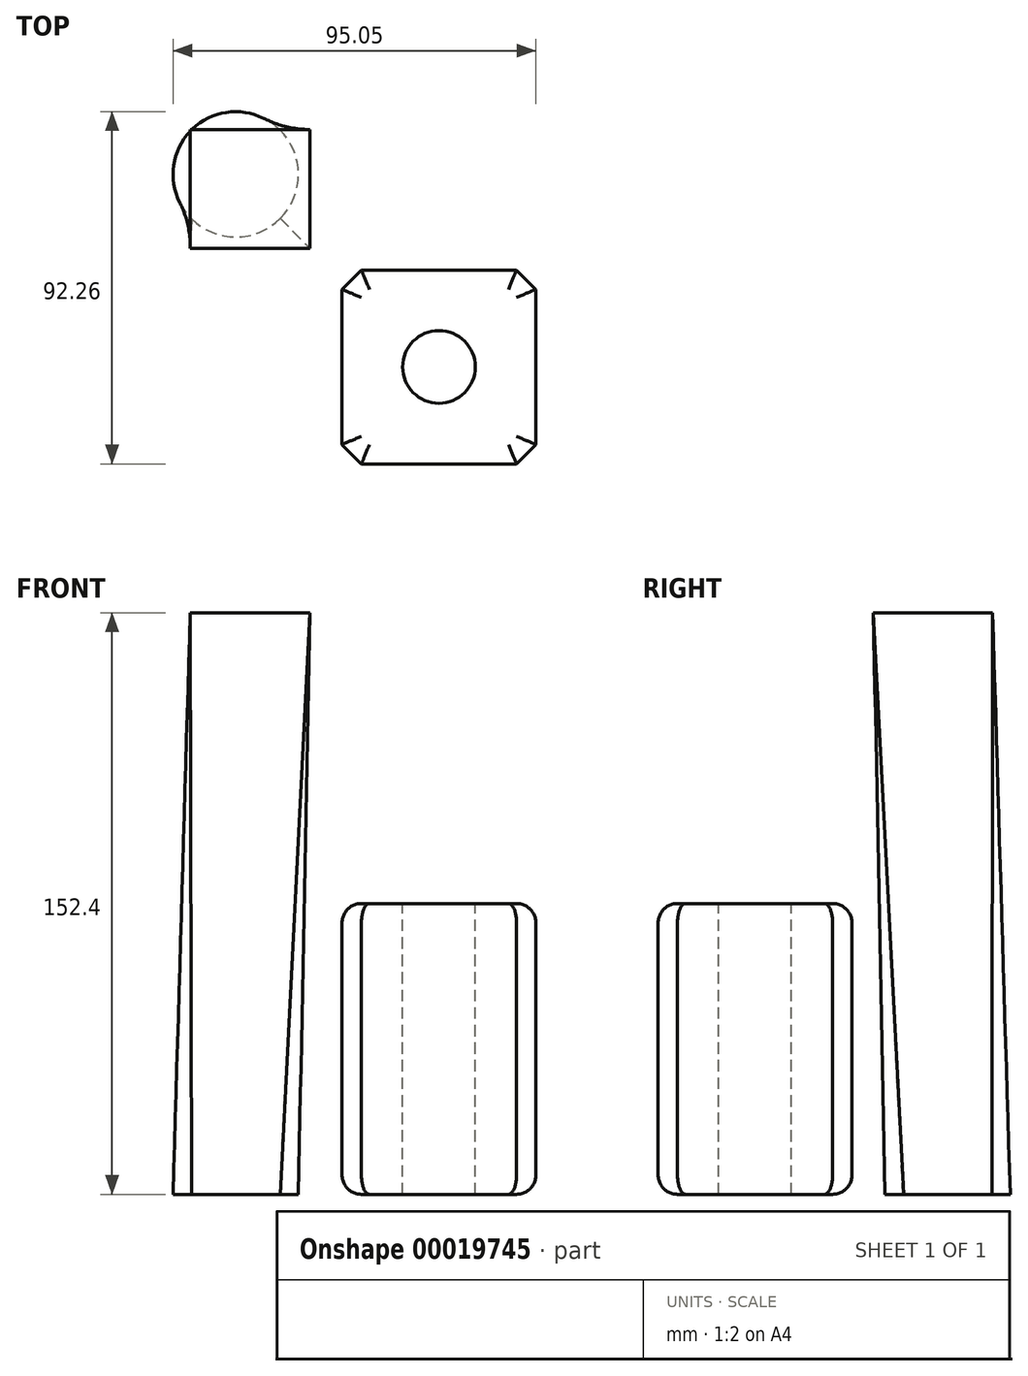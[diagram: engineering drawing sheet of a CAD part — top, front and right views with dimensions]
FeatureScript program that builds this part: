
annotation { "Feature Type Name" : "Feature", "Feature Type Description" : "" }
export const myFeature = defineFeature(function(context is Context, id is Id, definition is map)
    precondition{}
    {
        {
            var Q0;
            Q0=qCreatedBy(makeId("Top.planeOp"),FACE);
            var sketch = newSketch(context, id + "F0", { "sketchPlane" : qUnion([Q0])});
            skLineSegment(sketch, "E0.rect.bottom", {"start": v(-25.4, 25.4) * mm, "end": v(25.4, 25.4) * mm});
            skLineSegment(sketch, "E0.rect.top", {"start": v(-25.4, -25.4) * mm, "end": v(25.4, -25.4) * mm});
            skLineSegment(sketch, "E0.rect.left", {"start": v(-25.4, 25.4) * mm, "end": v(-25.4, -25.4) * mm});
            skLineSegment(sketch, "E0.rect.right", {"start": v(25.4, 25.4) * mm, "end": v(25.4, -25.4) * mm});
            skPoint(sketch, "E0.rect.middle", {"position": v(0, 0) * mm});
            skSolve(sketch);
        }
        {
            var Q0;
            Q0 = qSketchRegion(id + "F0", true);
            extrude(context, id + "F1", {"entities" : qUnion([Q0]), "depth" : 76.2 * mm});
        }
        {
            var Q0;
            Q0=makeQuery(id+"F1.opExtrude","CAP_FACE",FACE,{"disambiguationData":[OSD([sQuery(id+"F0.wireOp",EDGE,"E0.rect.bottom"),sQuery(id+"F0.wireOp",EDGE,"E0.rect.top"),sQuery(id+"F0.wireOp",EDGE,"E0.rect.left"),sQuery(id+"F0.wireOp",EDGE,"E0.rect.right")])],"isStart":false});
            var sketch = newSketch(context, id + "F2", { "sketchPlane" : qUnion([Q0])});
            skCircle(sketch, "E1", {"center": v(0, 0) * mm, "radius": 9.53 * mm});
            skSolve(sketch);
        }
        {
            var Q0;
            Q0=makeQuery(id+"F2.imprint","IMPRINT",FACE,{"disambiguationData":[TD([[makeQuery(id+"F2.imprint","IMPRINT",EDGE,{"derivedFrom":sQuery(id+"F2.wireOp",EDGE,"E1")}),1.0]])]});
            extrude(context, id + "F3", {"entities" : qUnion([Q0]), "operationType" : NewBodyOperationType.REMOVE, "oppositeDirection" : true, "depth" : 123.9 * mm});
        }
        {
            var Q0;
            Q0=makeQuery(id+"F1.opExtrude","SWEPT_EDGE",EDGE,{"disambiguationData":[OSD([sQuery(id+"F0.wireOp",EDGE,"E0.rect.top"),sQuery(id+"F0.wireOp",EDGE,"E0.rect.left")])]});
            var Q1;
            Q1=makeQuery(id+"F1.opExtrude","SWEPT_EDGE",EDGE,{"disambiguationData":[OSD([sQuery(id+"F0.wireOp",EDGE,"E0.rect.top"),sQuery(id+"F0.wireOp",EDGE,"E0.rect.right")])]});
            var Q2;
            Q2=makeQuery(id+"F1.opExtrude","SWEPT_EDGE",EDGE,{"disambiguationData":[OSD([sQuery(id+"F0.wireOp",EDGE,"E0.rect.bottom"),sQuery(id+"F0.wireOp",EDGE,"E0.rect.right")])]});
            var Q3;
            Q3=makeQuery(id+"F1.opExtrude","SWEPT_EDGE",EDGE,{"disambiguationData":[OSD([sQuery(id+"F0.wireOp",EDGE,"E0.rect.bottom"),sQuery(id+"F0.wireOp",EDGE,"E0.rect.left")])]});
            chamfer(context, id + "F4", {"entities" : qUnion([Q0, Q1, Q2, Q3]), "width" : 5.08 * mm, "tangentPropagation" : true});
        }
        {
            var Q0;
            Q0=makeQuery(id+"F1.opExtrude","CAP_EDGE",EDGE,{"disambiguationData":[OSD([sQuery(id+"F0.wireOp",EDGE,"E0.rect.bottom")])],"isStart":false});
            var Q1;
            {var subQ0=sQuery(id+"F0.wireOp",EDGE,"E0.rect.bottom");var subQ1=sQuery(id+"F0.wireOp",EDGE,"E0.rect.left");Q1=makeQuery(id+"F4.opChamfer","BLEND_EDGE",EDGE,{"blendedFrom":[makeQuery(id+"F1.opExtrude","SWEPT_EDGE",EDGE,{"disambiguationData":[OSD([subQ0,subQ1])]}),makeQuery(id+"F1.opExtrude","CAP_FACE",FACE,{"disambiguationData":[OSD([subQ0,sQuery(id+"F0.wireOp",EDGE,"E0.rect.top"),subQ1,sQuery(id+"F0.wireOp",EDGE,"E0.rect.right")])],"isStart":false})],"blendedInto":[makeQuery(id+"F1.opExtrude","CAP_FACE",FACE,{"disambiguationData":[OSD([subQ0,sQuery(id+"F0.wireOp",EDGE,"E0.rect.top"),subQ1,sQuery(id+"F0.wireOp",EDGE,"E0.rect.right")])],"isStart":false})]});}
            var Q2;
            Q2=makeQuery(id+"F1.opExtrude","CAP_EDGE",EDGE,{"disambiguationData":[OSD([sQuery(id+"F0.wireOp",EDGE,"E0.rect.left")])],"isStart":false});
            var Q3;
            Q3=makeQuery(id+"F1.opExtrude","CAP_EDGE",EDGE,{"disambiguationData":[OSD([sQuery(id+"F0.wireOp",EDGE,"E0.rect.top")])],"isStart":false});
            var Q4;
            Q4=makeQuery(id+"F1.opExtrude","CAP_EDGE",EDGE,{"disambiguationData":[OSD([sQuery(id+"F0.wireOp",EDGE,"E0.rect.right")])],"isStart":false});
            var Q5;
            {var subQ0=sQuery(id+"F0.wireOp",EDGE,"E0.rect.bottom");var subQ1=sQuery(id+"F0.wireOp",EDGE,"E0.rect.right");Q5=makeQuery(id+"F4.opChamfer","BLEND_EDGE",EDGE,{"blendedFrom":[makeQuery(id+"F1.opExtrude","SWEPT_EDGE",EDGE,{"disambiguationData":[OSD([subQ0,subQ1])]}),makeQuery(id+"F1.opExtrude","CAP_FACE",FACE,{"disambiguationData":[OSD([subQ0,sQuery(id+"F0.wireOp",EDGE,"E0.rect.top"),sQuery(id+"F0.wireOp",EDGE,"E0.rect.left"),subQ1])],"isStart":false})],"blendedInto":[makeQuery(id+"F1.opExtrude","CAP_FACE",FACE,{"disambiguationData":[OSD([subQ0,sQuery(id+"F0.wireOp",EDGE,"E0.rect.top"),sQuery(id+"F0.wireOp",EDGE,"E0.rect.left"),subQ1])],"isStart":false})]});}
            var Q6;
            {var subQ0=sQuery(id+"F0.wireOp",EDGE,"E0.rect.top");var subQ1=sQuery(id+"F0.wireOp",EDGE,"E0.rect.right");Q6=makeQuery(id+"F4.opChamfer","BLEND_EDGE",EDGE,{"blendedFrom":[makeQuery(id+"F1.opExtrude","SWEPT_EDGE",EDGE,{"disambiguationData":[OSD([subQ0,subQ1])]}),makeQuery(id+"F1.opExtrude","CAP_FACE",FACE,{"disambiguationData":[OSD([sQuery(id+"F0.wireOp",EDGE,"E0.rect.bottom"),subQ0,sQuery(id+"F0.wireOp",EDGE,"E0.rect.left"),subQ1])],"isStart":false})],"blendedInto":[makeQuery(id+"F1.opExtrude","CAP_FACE",FACE,{"disambiguationData":[OSD([sQuery(id+"F0.wireOp",EDGE,"E0.rect.bottom"),subQ0,sQuery(id+"F0.wireOp",EDGE,"E0.rect.left"),subQ1])],"isStart":false})]});}
            var Q7;
            {var subQ0=sQuery(id+"F0.wireOp",EDGE,"E0.rect.top");var subQ1=sQuery(id+"F0.wireOp",EDGE,"E0.rect.left");Q7=makeQuery(id+"F4.opChamfer","BLEND_EDGE",EDGE,{"blendedFrom":[makeQuery(id+"F1.opExtrude","SWEPT_EDGE",EDGE,{"disambiguationData":[OSD([subQ0,subQ1])]}),makeQuery(id+"F1.opExtrude","CAP_FACE",FACE,{"disambiguationData":[OSD([sQuery(id+"F0.wireOp",EDGE,"E0.rect.bottom"),subQ0,subQ1,sQuery(id+"F0.wireOp",EDGE,"E0.rect.right")])],"isStart":false})],"blendedInto":[makeQuery(id+"F1.opExtrude","CAP_FACE",FACE,{"disambiguationData":[OSD([sQuery(id+"F0.wireOp",EDGE,"E0.rect.bottom"),subQ0,subQ1,sQuery(id+"F0.wireOp",EDGE,"E0.rect.right")])],"isStart":false})]});}
            fillet(context, id + "F5", {"entities" : qUnion([Q0, Q1, Q2, Q3, Q4, Q5, Q6, Q7]), "radius" : 5.08 * mm, "tangentPropagation" : true, "allowEdgeOverflow" : false});
        }
        {
            var Q0;
            {var subQ0=sQuery(id+"F0.wireOp",EDGE,"E0.rect.top");var subQ1=sQuery(id+"F0.wireOp",EDGE,"E0.rect.left");Q0=makeQuery(id+"F4.opChamfer","BLEND_EDGE",EDGE,{"blendedFrom":[makeQuery(id+"F1.opExtrude","SWEPT_EDGE",EDGE,{"disambiguationData":[OSD([subQ0,subQ1])]}),makeQuery(id+"F1.opExtrude","CAP_FACE",FACE,{"disambiguationData":[OSD([sQuery(id+"F0.wireOp",EDGE,"E0.rect.bottom"),subQ0,subQ1,sQuery(id+"F0.wireOp",EDGE,"E0.rect.right")])],"isStart":true})],"blendedInto":[makeQuery(id+"F1.opExtrude","CAP_FACE",FACE,{"disambiguationData":[OSD([sQuery(id+"F0.wireOp",EDGE,"E0.rect.bottom"),subQ0,subQ1,sQuery(id+"F0.wireOp",EDGE,"E0.rect.right")])],"isStart":true})]});}
            var Q1;
            Q1=makeQuery(id+"F1.opExtrude","CAP_EDGE",EDGE,{"disambiguationData":[OSD([sQuery(id+"F0.wireOp",EDGE,"E0.rect.left")])],"isStart":true});
            var Q2;
            Q2=makeQuery(id+"F1.opExtrude","CAP_EDGE",EDGE,{"disambiguationData":[OSD([sQuery(id+"F0.wireOp",EDGE,"E0.rect.top")])],"isStart":true});
            var Q3;
            {var subQ0=sQuery(id+"F0.wireOp",EDGE,"E0.rect.top");var subQ1=sQuery(id+"F0.wireOp",EDGE,"E0.rect.right");Q3=makeQuery(id+"F4.opChamfer","BLEND_EDGE",EDGE,{"blendedFrom":[makeQuery(id+"F1.opExtrude","SWEPT_EDGE",EDGE,{"disambiguationData":[OSD([subQ0,subQ1])]}),makeQuery(id+"F1.opExtrude","CAP_FACE",FACE,{"disambiguationData":[OSD([sQuery(id+"F0.wireOp",EDGE,"E0.rect.bottom"),subQ0,sQuery(id+"F0.wireOp",EDGE,"E0.rect.left"),subQ1])],"isStart":true})],"blendedInto":[makeQuery(id+"F1.opExtrude","CAP_FACE",FACE,{"disambiguationData":[OSD([sQuery(id+"F0.wireOp",EDGE,"E0.rect.bottom"),subQ0,sQuery(id+"F0.wireOp",EDGE,"E0.rect.left"),subQ1])],"isStart":true})]});}
            var Q4;
            Q4=makeQuery(id+"F1.opExtrude","CAP_EDGE",EDGE,{"disambiguationData":[OSD([sQuery(id+"F0.wireOp",EDGE,"E0.rect.right")])],"isStart":true});
            var Q5;
            {var subQ0=sQuery(id+"F0.wireOp",EDGE,"E0.rect.bottom");var subQ1=sQuery(id+"F0.wireOp",EDGE,"E0.rect.right");Q5=makeQuery(id+"F4.opChamfer","BLEND_EDGE",EDGE,{"blendedFrom":[makeQuery(id+"F1.opExtrude","SWEPT_EDGE",EDGE,{"disambiguationData":[OSD([subQ0,subQ1])]}),makeQuery(id+"F1.opExtrude","CAP_FACE",FACE,{"disambiguationData":[OSD([subQ0,sQuery(id+"F0.wireOp",EDGE,"E0.rect.top"),sQuery(id+"F0.wireOp",EDGE,"E0.rect.left"),subQ1])],"isStart":true})],"blendedInto":[makeQuery(id+"F1.opExtrude","CAP_FACE",FACE,{"disambiguationData":[OSD([subQ0,sQuery(id+"F0.wireOp",EDGE,"E0.rect.top"),sQuery(id+"F0.wireOp",EDGE,"E0.rect.left"),subQ1])],"isStart":true})]});}
            var Q6;
            Q6=makeQuery(id+"F1.opExtrude","CAP_EDGE",EDGE,{"disambiguationData":[OSD([sQuery(id+"F0.wireOp",EDGE,"E0.rect.bottom")])],"isStart":true});
            var Q7;
            {var subQ0=sQuery(id+"F0.wireOp",EDGE,"E0.rect.bottom");var subQ1=sQuery(id+"F0.wireOp",EDGE,"E0.rect.left");Q7=makeQuery(id+"F4.opChamfer","BLEND_EDGE",EDGE,{"blendedFrom":[makeQuery(id+"F1.opExtrude","SWEPT_EDGE",EDGE,{"disambiguationData":[OSD([subQ0,subQ1])]}),makeQuery(id+"F1.opExtrude","CAP_FACE",FACE,{"disambiguationData":[OSD([subQ0,sQuery(id+"F0.wireOp",EDGE,"E0.rect.top"),subQ1,sQuery(id+"F0.wireOp",EDGE,"E0.rect.right")])],"isStart":true})],"blendedInto":[makeQuery(id+"F1.opExtrude","CAP_FACE",FACE,{"disambiguationData":[OSD([subQ0,sQuery(id+"F0.wireOp",EDGE,"E0.rect.top"),subQ1,sQuery(id+"F0.wireOp",EDGE,"E0.rect.right")])],"isStart":true})]});}
            fillet(context, id + "F6", {"entities" : qUnion([Q0, Q1, Q2, Q3, Q4, Q5, Q6, Q7]), "radius" : 5.08 * mm, "tangentPropagation" : true, "allowEdgeOverflow" : false});
        }
        {
            var Q0;
            Q0=qCreatedBy(makeId("Top.planeOp"),FACE);
            cPlane(context, id + "F7", {"entities" : qUnion([Q0]), "cplaneType" : CPlaneType.OFFSET, "offset" : 152.4 * mm, "width" : 152.4 * mm, "height" : 152.4 * mm});
        }
        {
            var Q0;
            Q0=qCreatedBy(id+"F7.planeOp",FACE);
            var sketch = newSketch(context, id + "F8", { "sketchPlane" : qUnion([Q0])});
            skLineSegment(sketch, "E2.bottom", {"start": v(-65.17, 62.22) * mm, "end": v(-33.79, 62.22) * mm});
            skLineSegment(sketch, "E2.top", {"start": v(-65.17, 31.01) * mm, "end": v(-33.79, 31.01) * mm});
            skLineSegment(sketch, "E2.left", {"start": v(-65.17, 62.22) * mm, "end": v(-65.17, 31.01) * mm});
            skLineSegment(sketch, "E2.right", {"start": v(-33.79, 62.22) * mm, "end": v(-33.79, 31.01) * mm});
            skSolve(sketch);
        }
        {
            var Q0;
            Q0=qCreatedBy(makeId("Top.planeOp"),FACE);
            var sketch = newSketch(context, id + "F9", { "sketchPlane" : qUnion([Q0])});
            skCircle(sketch, "E3", {"center": v(-53.24, 50.44) * mm, "radius": 16.42 * mm});
            skPoint(sketch, "E3.first.point", {"position": v(-55.77, 34.22) * mm});
            skPoint(sketch, "E3.second.point", {"position": v(-49.24, 66.36) * mm});
            skPoint(sketch, "E3.third.point", {"position": v(-69.28, 46.96) * mm});
            skSolve(sketch);
        }
        {
            var Q0;
            Q0=makeQuery(id+"F9.imprint","IMPRINT",FACE,{"disambiguationData":[TD([[makeQuery(id+"F9.imprint","IMPRINT",EDGE,{"derivedFrom":sQuery(id+"F9.wireOp",EDGE,"E3")}),1.0]])]});
            var Q1;
            Q1=makeQuery(id+"F8.imprint","IMPRINT",FACE,{"disambiguationData":[TD([[makeQuery(id+"F8.imprint","IMPRINT",EDGE,{"derivedFrom":sQuery(id+"F8.wireOp",EDGE,"E2.bottom")}),-1.0]])]});
            loft(context, id + "F10", {"sheetProfilesArray" : [{ "sheetProfileEntities" : qUnion([Q0]) }, { "sheetProfileEntities" : qUnion([Q1]) }]});
        }
    });
